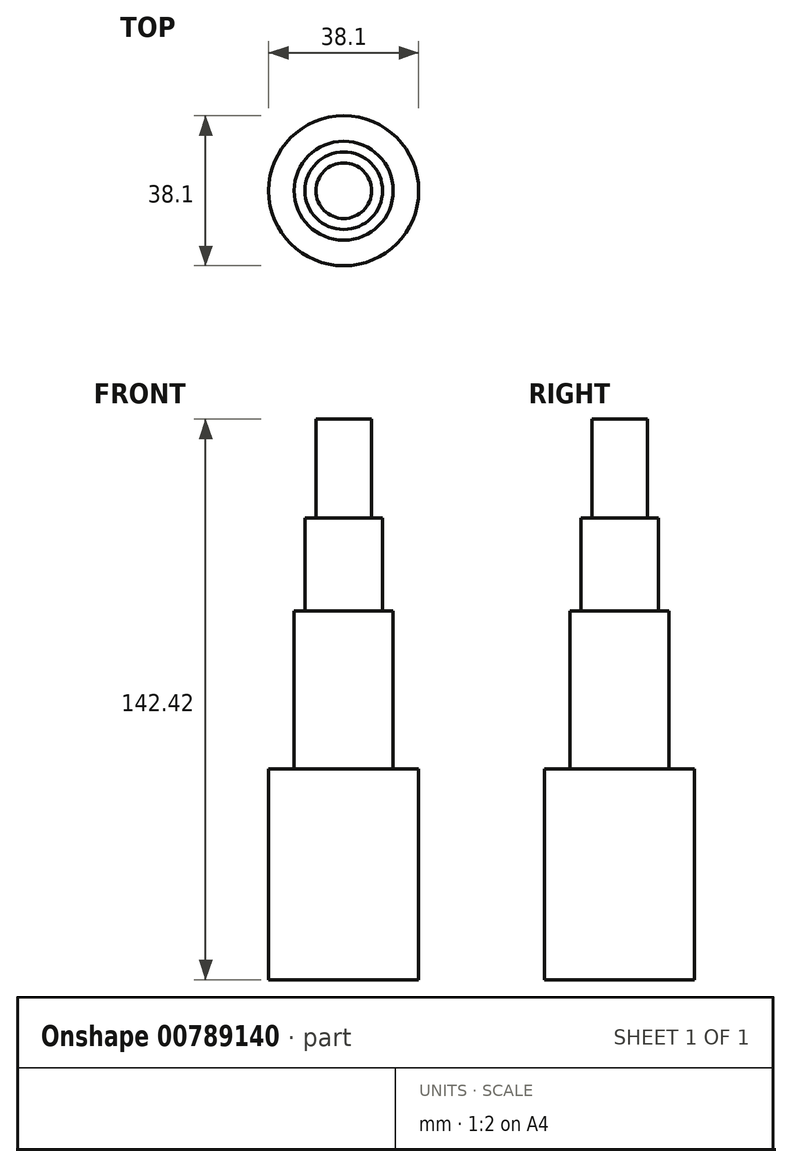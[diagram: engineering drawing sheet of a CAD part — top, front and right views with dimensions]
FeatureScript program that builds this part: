
annotation { "Feature Type Name" : "Feature", "Feature Type Description" : "" }
export const myFeature = defineFeature(function(context is Context, id is Id, definition is map)
    precondition{}
    {
        {
            var Q0;
            Q0=qCreatedBy(makeId("Top.planeOp"),FACE);
            var sketch = newSketch(context, id + "F0", { "sketchPlane" : qUnion([Q0])});
            skCircle(sketch, "E0", {"center": v(0, 0) * mm, "radius": 19.05 * mm});
            skSolve(sketch);
        }
        {
            var Q0;
            Q0=makeQuery(id+"F0.imprint","IMPRINT",FACE,{"disambiguationData":[TD([[makeQuery(id+"F0.imprint","IMPRINT",EDGE,{"derivedFrom":sQuery(id+"F0.wireOp",EDGE,"E0")}),1.0]])]});
            extrude(context, id + "F1", {"entities" : qUnion([Q0]), "depth" : 53.6 * mm, "offsetDistance" : 25.4 * mm});
        }
        {
            var Q0;
            Q0=makeQuery(id+"F1.opExtrude","CAP_FACE",FACE,{"disambiguationData":[OSD([sQuery(id+"F0.wireOp",EDGE,"E0")])],"isStart":false});
            var sketch = newSketch(context, id + "F2", { "sketchPlane" : qUnion([Q0])});
            skCircle(sketch, "E1", {"center": v(0, 0) * mm, "radius": 12.57 * mm});
            skSolve(sketch);
        }
        {
            var Q0;
            Q0=makeQuery(id+"F2.imprint","IMPRINT",FACE,{"disambiguationData":[TD([[makeQuery(id+"F2.imprint","IMPRINT",EDGE,{"derivedFrom":sQuery(id+"F2.wireOp",EDGE,"E1")}),1.0]])]});
            extrude(context, id + "F3", {"entities" : qUnion([Q0]), "operationType" : NewBodyOperationType.ADD, "depth" : 40.13 * mm, "offsetDistance" : 25.4 * mm});
        }
        {
            var Q0;
            Q0=makeQuery(id+"F3.opExtrude","CAP_FACE",FACE,{"disambiguationData":[OSD([sQuery(id+"F2.wireOp",EDGE,"E1")])],"isStart":false});
            var sketch = newSketch(context, id + "F4", { "sketchPlane" : qUnion([Q0])});
            skCircle(sketch, "E2", {"center": v(0, 0) * mm, "radius": 9.86 * mm});
            skSolve(sketch);
        }
        {
            var Q0;
            Q0=makeQuery(id+"F4.imprint","IMPRINT",FACE,{"disambiguationData":[TD([[makeQuery(id+"F4.imprint","IMPRINT",EDGE,{"derivedFrom":sQuery(id+"F4.wireOp",EDGE,"E2")}),1.0]])]});
            extrude(context, id + "F5", {"entities" : qUnion([Q0]), "operationType" : NewBodyOperationType.ADD, "depth" : 23.55 * mm, "offsetDistance" : 25.4 * mm});
        }
        {
            var Q0;
            Q0=makeQuery(id+"F5.opExtrude","CAP_FACE",FACE,{"disambiguationData":[OSD([sQuery(id+"F4.wireOp",EDGE,"E2")])],"isStart":false});
            var sketch = newSketch(context, id + "F6", { "sketchPlane" : qUnion([Q0])});
            skCircle(sketch, "E3", {"center": v(0, 0) * mm, "radius": 7.06 * mm});
            skSolve(sketch);
        }
        {
            var Q0;
            Q0=makeQuery(id+"F6.imprint","IMPRINT",FACE,{"disambiguationData":[TD([[makeQuery(id+"F6.imprint","IMPRINT",EDGE,{"derivedFrom":sQuery(id+"F6.wireOp",EDGE,"E3")}),1.0]])]});
            extrude(context, id + "F7", {"entities" : qUnion([Q0]), "operationType" : NewBodyOperationType.ADD, "depth" : 25.15 * mm, "offsetDistance" : 25.4 * mm});
        }
    });
